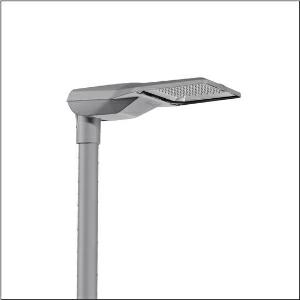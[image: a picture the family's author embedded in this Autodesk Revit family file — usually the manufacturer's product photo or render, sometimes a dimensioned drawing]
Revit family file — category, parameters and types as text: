
# Revit family: streetlight_sl_21_iq_midi___st0_5a_5xe3b41g08mb_6195
name_source: partatom
category: Lighting Fixtures
units: mm (PartAtom-declared; Revit-internal decimal feet)

## family parameters
Cut with Voids When Loaded = No
Host = Face
Light Source = No
Part Type = Normal
Room Calculation Point = No
Round Connector Dimension = Use Diameter
Shared = No

## types (1)
- --- (1 x LED, 20360 lm, 146.7 W, 4000K)
    Apparent Load = 147 VA
    CIE Flux Codes = 41 75 97 100 100
    Color Rendering = 70
    Color Temperature = 4000K
    Default Elevation = 1800 mm
    Description = Streetlight SL 21 iQ midi, mast luminaire, primary light control with lens, of PMMA, primary optical cover: cover, of toughened safety glass, transparent, light distribution: ST0.5a, light emission: direct distribution, primary light characteristic: asymmetric, installation type: post-top, side-entry, LED, High Power LED, rated luminous flux: 20.360lm, luminous efficacy: 139lm/W, light colour: 740, colour temperature: 4000K, control: Street-Remote, Auto-Match, Temp-Guard, Lumen-Switch, Night-Set, Smart-Wire, Light-Fading, Desk-Remote (wireless, voltage-free reading and setting of iQ features in the workshop via application-optimized NFC function/RFID function), optimised constant luminous flux control (CLO 2.0), presetting dimming linear, mains connection: 230..240V, AC, 50/60Hz, start of lifetime: 147W, end of service life: 161W, reduction: 62W, luminaire housing, of diecast aluminium, powder-coated, Siteco® metallic grey (DB 702S), corrosivity category C5 mid according to DIN EN ISO 12944, please order mast flange separately, inclination adjustable: 0°, 5°, 10°, 15°, sealing non-destructively replaceable, multi-level sealing system, length: 644mm, width: 335mm, height: 110mm, mast flange for spigot size: 42mm (side-entry): 5XC10008XM4, 60/48mm (side-entry/post-top): 5XC10108XM2, 76/60mm (side-entry/post-top): 5XC10108XM1, protection rating (complete): IP66, insulation class (complete): insulation class II (safety insulation), certification: CE, ENEC, ENEC+, VDE, impact resistance: IK09, permissible operating ambient temperature for outdoor applications: -40..+50°C, standard-compliant lighting for roads and squares, packaging unit: 1 piece

Light Distribution: ST0.5a
    Height = 111 mm
    Lamp = 1 x LED
    Lamp Light Flux = 20360 lm
    Lamp Power = 146.7 W
    Lamp count = 1
    Length = 644 mm
    Luminous efficacy = 139 lm/W
    Manufacturer = Siteco
    ModVariant = No
    Model = 5XE3B41G08MB
    Number of Poles = 1
    OnlyDefault = Yes
    Power Factor = 1
    Product Name = Streetlight SL 21 iQ midi | ST0.5a
    Product group = mast luminaire | pylon top
    ProductGroupID = 6100
    Protection Class = Protection class II
    Protection Degree = IP 66
    RLX_Detail_Level = 1
    RLX_Emergency_Light_Flux = 0 lm
    RLX_Emergency_Type = 0
    RLX_Emergency_Type_DB = No
    RlxData = <blob elided: 101785 chars, md5=1d6d88fa>
    Socket = socket
    Standby Power = 0 W
    System Light Flux = 20360 lm
    System Power = 147 W
    Type Comments = factory setting: luminous flux: 100 % | dim-lin: 254 | 753 mA
    Type Image = l_1004298.jpg
    URL = http://relux.com
    VarID = @adj_144387
    Voltage = 0 V
    Weight = 0.00 kg
    Width = 336 mm

## geometry (parser evidence)
native form markers: Blend x4, Sweep x11
no freeform markers — native parametric forms only
